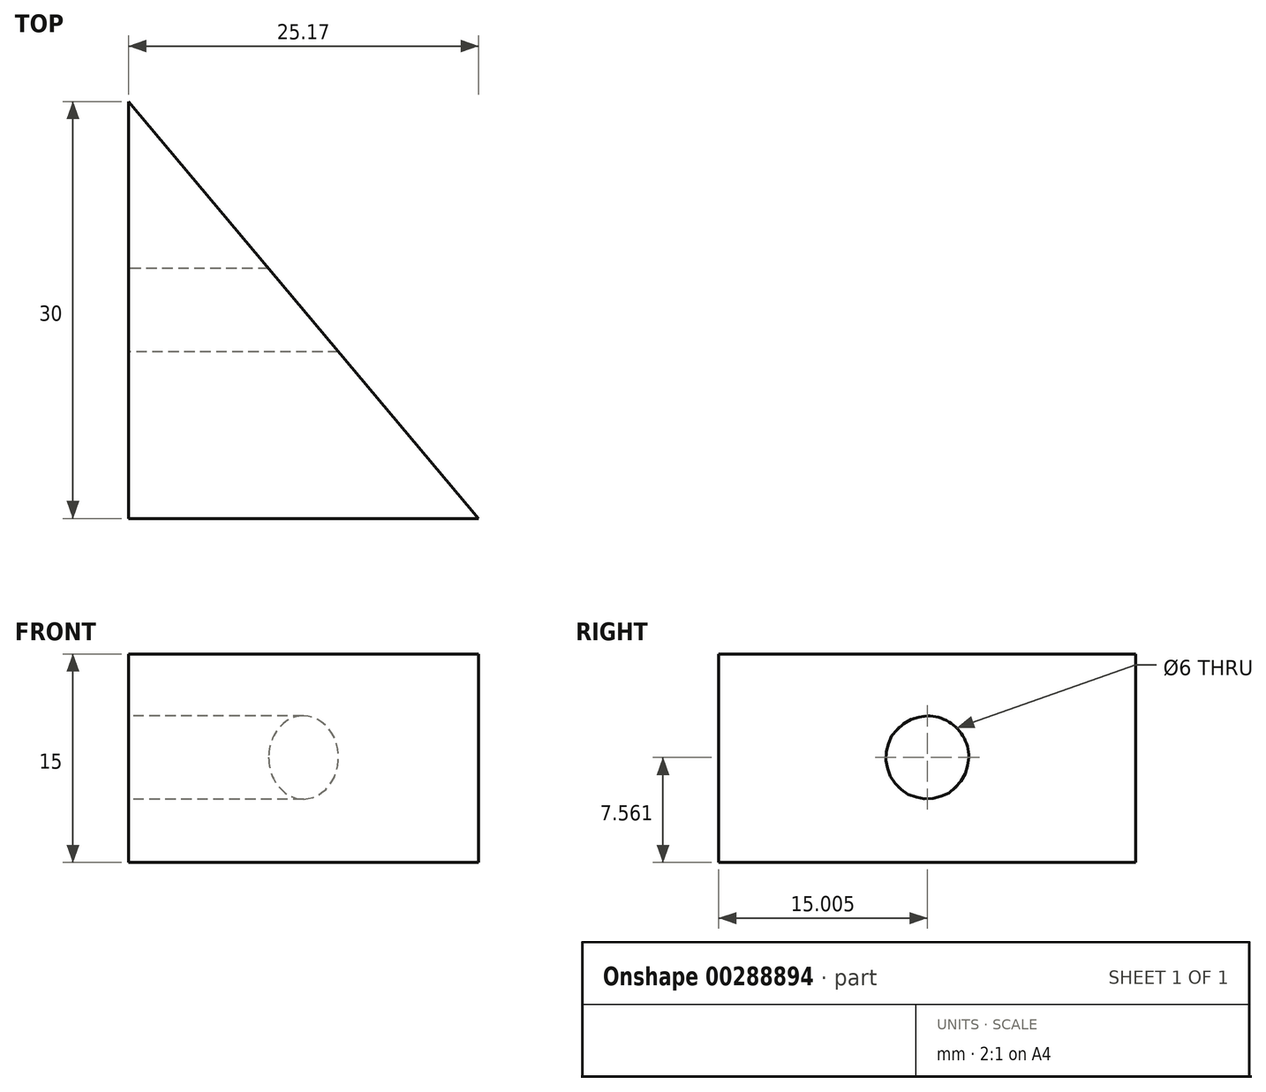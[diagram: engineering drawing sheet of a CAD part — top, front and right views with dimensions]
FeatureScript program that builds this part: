
annotation { "Feature Type Name" : "Feature", "Feature Type Description" : "" }
export const myFeature = defineFeature(function(context is Context, id is Id, definition is map)
    precondition{}
    {
        {
            var Q0;
            Q0=qCreatedBy(makeId("Top.planeOp"),FACE);
            var sketch = newSketch(context, id + "F0", { "sketchPlane" : qUnion([Q0])});
            skLineSegment(sketch, "E0", {"start": v(0, 45.26) * mm, "end": v(0, 15.26) * mm});
            skLineSegment(sketch, "E1", {"start": v(0, 15.26) * mm, "end": v(25.17, 15.26) * mm});
            skLineSegment(sketch, "E2", {"start": v(25.17, 15.26) * mm, "end": v(0, 45.26) * mm});
            skSolve(sketch);
        }
        {
            var Q0;
            Q0=qSketchRegion(id+"F0",true);
            extrude(context, id + "F1", {"entities" : qUnion([Q0]), "depth" : 15 * mm});
        }
        {
            var Q0;
            Q0=qCreatedBy(makeId("Right.planeOp"),FACE);
            var sketch = newSketch(context, id + "F2", { "sketchPlane" : qUnion([Q0])});
            skPoint(sketch, "E3", {"position": v(30.26, 7.56) * mm});
            skLineSegment(sketch, "E4", {"start": v(30.26, 7.56) * mm, "end": v(30.26, 0) * mm, "construction": true});
            skLineSegment(sketch, "E5", {"start": v(30.26, 7.56) * mm, "end": v(30.26, 15.12) * mm, "construction": true});
            skSolve(sketch);
        }
        {
            var Q0;
            Q0=sQuery(id+"F2.wireOp",VERTEX,"E3");
            var Q1;
            Q1=makeQuery(id+"F1.opExtrude","SWEPT_BODY",BODY,{"disambiguationData":[OSD([sQuery(id+"F0.wireOp",EDGE,"E0"),sQuery(id+"F0.wireOp",EDGE,"E1"),sQuery(id+"F0.wireOp",EDGE,"E2")])]});
            hole(context, id + "F3", {"style" : HoleStyle.SIMPLE, "endStyle" : HoleEndStyle.THROUGH, "oppositeDirection" : true, "holeDiameter" : 6 * mm, "tappedDepth" : 12 * mm, "tapClearance" : 3, "locations" : qUnion([Q0]), "scope" : qUnion([Q1])});
        }
    });
